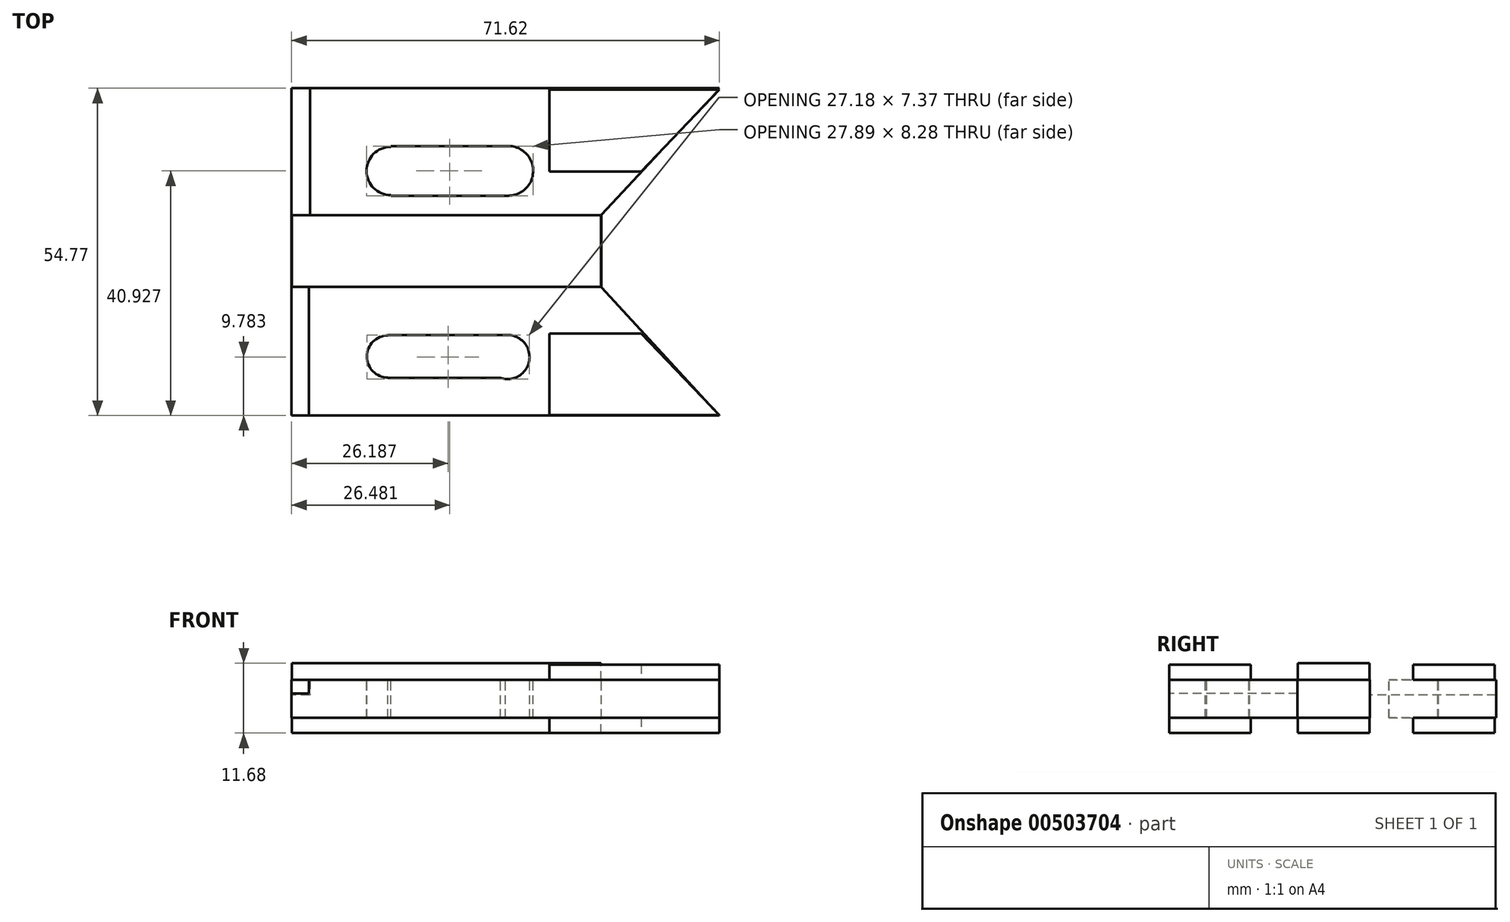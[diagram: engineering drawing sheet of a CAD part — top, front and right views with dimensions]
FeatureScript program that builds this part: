
annotation { "Feature Type Name" : "Feature", "Feature Type Description" : "" }
export const myFeature = defineFeature(function(context is Context, id is Id, definition is map)
    precondition{}
    {
        {
            var Q0;
            Q0=qCreatedBy(makeId("Top.planeOp"),FACE);
            var sketch = newSketch(context, id + "F0", { "sketchPlane" : qUnion([Q0])});
            skLineSegment(sketch, "E0", {"start": v(-35.97, 27.24) * mm, "end": v(-35.97, 13.58) * mm});
            skLineSegment(sketch, "E1", {"start": v(-35.97, 13.58) * mm, "end": v(-20.58, 13.58) * mm});
            skLineSegment(sketch, "E2", {"start": v(-20.58, 13.58) * mm, "end": v(-7.5, 27.24) * mm});
            skLineSegment(sketch, "E3", {"start": v(-7.5, 27.24) * mm, "end": v(-35.97, 27.24) * mm});
            skSolve(sketch);
        }
        {
            var Q0;
            Q0=makeQuery(id+"F0.imprint","IMPRINT",FACE,{"disambiguationData":[TD([[makeQuery(id+"F0.imprint","IMPRINT",EDGE,{"derivedFrom":sQuery(id+"F0.wireOp",EDGE,"E0")}),1.0]])]});
            var Q1;
            Q1 = qSketchRegion(id + "F0", true);
            extrude(context, id + "F1", {"entities" : qUnion([Q0, Q1]), "depth" : 2.54 * mm});
        }
        {
            var Q0;
            Q0=makeQuery(id+"F1.opExtrude","SWEPT_BODY",BODY,{"disambiguationData":[OSD([sQuery(id+"F0.wireOp",EDGE,"E0"),sQuery(id+"F0.wireOp",EDGE,"E1"),sQuery(id+"F0.wireOp",EDGE,"E2"),sQuery(id+"F0.wireOp",EDGE,"E3")])]});
            var Q1;
            Q1=qCreatedBy(makeId("Front.planeOp"),FACE);
            mirror(context, id + "F2", {"entities" : qUnion([Q0]), "mirrorPlane" : qUnion([Q1])});
        }
        {
            var Q0;
            Q0=qCreatedBy(makeId("Top.planeOp"),FACE);
            var sketch = newSketch(context, id + "F3", { "sketchPlane" : qUnion([Q0])});
            skLineSegment(sketch, "E4", {"start": v(-7.52, 27.5) * mm, "end": v(-27.27, 6.34) * mm});
            skLineSegment(sketch, "E5", {"start": v(-27.27, 6.34) * mm, "end": v(-27.27, -5.8) * mm});
            skLineSegment(sketch, "E6", {"start": v(-27.27, -5.8) * mm, "end": v(-7.52, -27.27) * mm});
            skLineSegment(sketch, "E7", {"start": v(-7.52, -27.27) * mm, "end": v(-79.12, -27.27) * mm});
            skLineSegment(sketch, "E8", {"start": v(-79.12, -27.27) * mm, "end": v(-79.12, 27.5) * mm});
            skLineSegment(sketch, "E9", {"start": v(-79.12, 27.5) * mm, "end": v(-7.52, 27.5) * mm});
            skSolve(sketch);
        }
        {
            var Q0;
            Q0 = qSketchRegion(id + "F3", true);
            extrude(context, id + "F4", {"entities" : qUnion([Q0]), "oppositeDirection" : true, "depth" : 6.35 * mm});
        }
        {
            var Q0;
            Q0=qCreatedBy(makeId("Top.planeOp"),FACE);
            cPlane(context, id + "F5", {"entities" : qUnion([Q0]), "cplaneType" : CPlaneType.OFFSET, "offset" : 2.8 * mm, "width" : 152.4 * mm, "height" : 152.4 * mm});
        }
        {
            var Q0;
            Q0=makeQuery(id+"F1.opExtrude","SWEPT_BODY",BODY,{"disambiguationData":[OSD([sQuery(id+"F0.wireOp",EDGE,"E0"),sQuery(id+"F0.wireOp",EDGE,"E1"),sQuery(id+"F0.wireOp",EDGE,"E2"),sQuery(id+"F0.wireOp",EDGE,"E3")])]});
            transform(context, id + "F6", {"entities" : qUnion([Q0]), "transformType" : TransformType.TRANSLATION_3D, "dx" : 0 * mm, "dy" : 0 * mm, "dz" : -8.9 * mm, "makeCopy" : true});
        }
        {
            var Q0;
            Q0=makeQuery(id+"F2.opPattern","COPY",BODY,{"derivedFrom":makeQuery(id+"F1.opExtrude","SWEPT_BODY",BODY,{"disambiguationData":[OSD([sQuery(id+"F0.wireOp",EDGE,"E0"),sQuery(id+"F0.wireOp",EDGE,"E1"),sQuery(id+"F0.wireOp",EDGE,"E2"),sQuery(id+"F0.wireOp",EDGE,"E3")])]}),"instanceName":"1"});
            transform(context, id + "F7", {"entities" : qUnion([Q0]), "transformType" : TransformType.TRANSLATION_3D, "dx" : 0 * mm, "dy" : 0 * mm, "dz" : -8.9 * mm, "makeCopy" : true});
        }
        {
            var Q0;
            Q0=qCreatedBy(id+"F5.planeOp",FACE);
            var sketch = newSketch(context, id + "F8", { "sketchPlane" : qUnion([Q0])});
            skLineSegment(sketch, "E10.bottom", {"start": v(-27.32, 6.27) * mm, "end": v(-79.08, 6.27) * mm});
            skLineSegment(sketch, "E10.top", {"start": v(-27.32, -5.74) * mm, "end": v(-79.08, -5.74) * mm});
            skLineSegment(sketch, "E10.left", {"start": v(-27.32, 6.27) * mm, "end": v(-27.32, -5.74) * mm});
            skLineSegment(sketch, "E10.right", {"start": v(-79.08, 6.27) * mm, "end": v(-79.08, -5.74) * mm});
            skSolve(sketch);
        }
        {
            var Q0;
            Q0=makeQuery(id+"F8.imprint","IMPRINT",FACE,{"disambiguationData":[TD([[makeQuery(id+"F8.imprint","IMPRINT",EDGE,{"derivedFrom":sQuery(id+"F8.wireOp",EDGE,"E10.bottom")}),1.0]])]});
            extrude(context, id + "F9", {"entities" : qUnion([Q0]), "operationType" : NewBodyOperationType.ADD, "oppositeDirection" : true, "depth" : 11.68 * mm});
        }
        {
            var Q0;
            Q0=qCreatedBy(makeId("Top.planeOp"),FACE);
            var sketch = newSketch(context, id + "F10", { "sketchPlane" : qUnion([Q0])});
            skLineSegment(sketch, "E11.bottom", {"start": v(-79.26, 27.64) * mm, "end": v(-76.06, 27.64) * mm});
            skLineSegment(sketch, "E11.top", {"start": v(-79.26, 6.25) * mm, "end": v(-76.06, 6.25) * mm});
            skLineSegment(sketch, "E11.left", {"start": v(-79.26, 27.64) * mm, "end": v(-79.26, 6.25) * mm});
            skLineSegment(sketch, "E11.right", {"start": v(-76.06, 27.64) * mm, "end": v(-76.06, 6.25) * mm});
            skSolve(sketch);
        }
        {
            var Q0;
            Q0 = qSketchRegion(id + "F10", true);
            extrude(context, id + "F11", {"entities" : qUnion([Q0]), "operationType" : NewBodyOperationType.REMOVE, "oppositeDirection" : true, "depth" : 2.54 * mm});
        }
        {
            var Q0;
            Q0=qCreatedBy(makeId("Top.planeOp"),FACE);
            var sketch = newSketch(context, id + "F12", { "sketchPlane" : qUnion([Q0])});
            skLineSegment(sketch, "E12.bottom", {"start": v(-76.24, -5.71) * mm, "end": v(-79.68, -5.71) * mm});
            skLineSegment(sketch, "E12.top", {"start": v(-76.24, -27.56) * mm, "end": v(-79.68, -27.56) * mm});
            skLineSegment(sketch, "E12.left", {"start": v(-76.24, -5.71) * mm, "end": v(-76.24, -27.56) * mm});
            skLineSegment(sketch, "E12.right", {"start": v(-79.68, -5.71) * mm, "end": v(-79.68, -27.56) * mm});
            skSolve(sketch);
        }
        {
            var Q0;
            Q0 = qSketchRegion(id + "F12", true);
            extrude(context, id + "F13", {"entities" : qUnion([Q0]), "operationType" : NewBodyOperationType.REMOVE, "oppositeDirection" : true, "depth" : 2.3 * mm});
        }
        {
            var Q0;
            Q0=qCreatedBy(id+"F5.planeOp",FACE);
            var sketch = newSketch(context, id + "F14", { "sketchPlane" : qUnion([Q0])});
            skCircle(sketch, "E13", {"center": v(-42.84, 13.67) * mm, "radius": 4.15 * mm});
            skLineSegment(sketch, "E14.bottom", {"start": v(-42.86, 9.52) * mm, "end": v(-62.54, 9.52) * mm});
            skLineSegment(sketch, "E14.top", {"start": v(-42.86, 17.8) * mm, "end": v(-62.54, 17.8) * mm});
            skLineSegment(sketch, "E14.left", {"start": v(-42.86, 9.52) * mm, "end": v(-42.86, 17.8) * mm});
            skLineSegment(sketch, "E14.right", {"start": v(-62.54, 9.52) * mm, "end": v(-62.54, 17.8) * mm});
            skCircle(sketch, "E15", {"center": v(-62.54, 13.66) * mm, "radius": 4.04 * mm});
            skSolve(sketch);
        }
        {
            var Q0;
            Q0 = qSketchRegion(id + "F14", true);
            extrude(context, id + "F15", {"entities" : qUnion([Q0]), "operationType" : NewBodyOperationType.REMOVE, "oppositeDirection" : true, "depth" : 25.4 * mm});
        }
        {
            var Q0;
            Q0=qCreatedBy(makeId("Top.planeOp"),FACE);
            var sketch = newSketch(context, id + "F16", { "sketchPlane" : qUnion([Q0])});
            skCircle(sketch, "E16", {"center": v(-43, -17.5) * mm, "radius": 3.7 * mm});
            skLineSegment(sketch, "E17.bottom", {"start": v(-43, -13.8) * mm, "end": v(-63, -13.8) * mm});
            skLineSegment(sketch, "E17.top", {"start": v(-43, -21.01) * mm, "end": v(-63, -21.01) * mm});
            skLineSegment(sketch, "E17.left", {"start": v(-43, -13.8) * mm, "end": v(-43, -21.01) * mm});
            skLineSegment(sketch, "E17.right", {"start": v(-63, -13.8) * mm, "end": v(-63, -21.01) * mm});
            skCircle(sketch, "E18", {"center": v(-63, -17.4) * mm, "radius": 3.52 * mm});
            skSolve(sketch);
        }
        {
            var Q0;
            Q0 = qSketchRegion(id + "F16", true);
            extrude(context, id + "F17", {"entities" : qUnion([Q0]), "operationType" : NewBodyOperationType.REMOVE, "oppositeDirection" : true, "depth" : 25.4 * mm});
        }
    });
